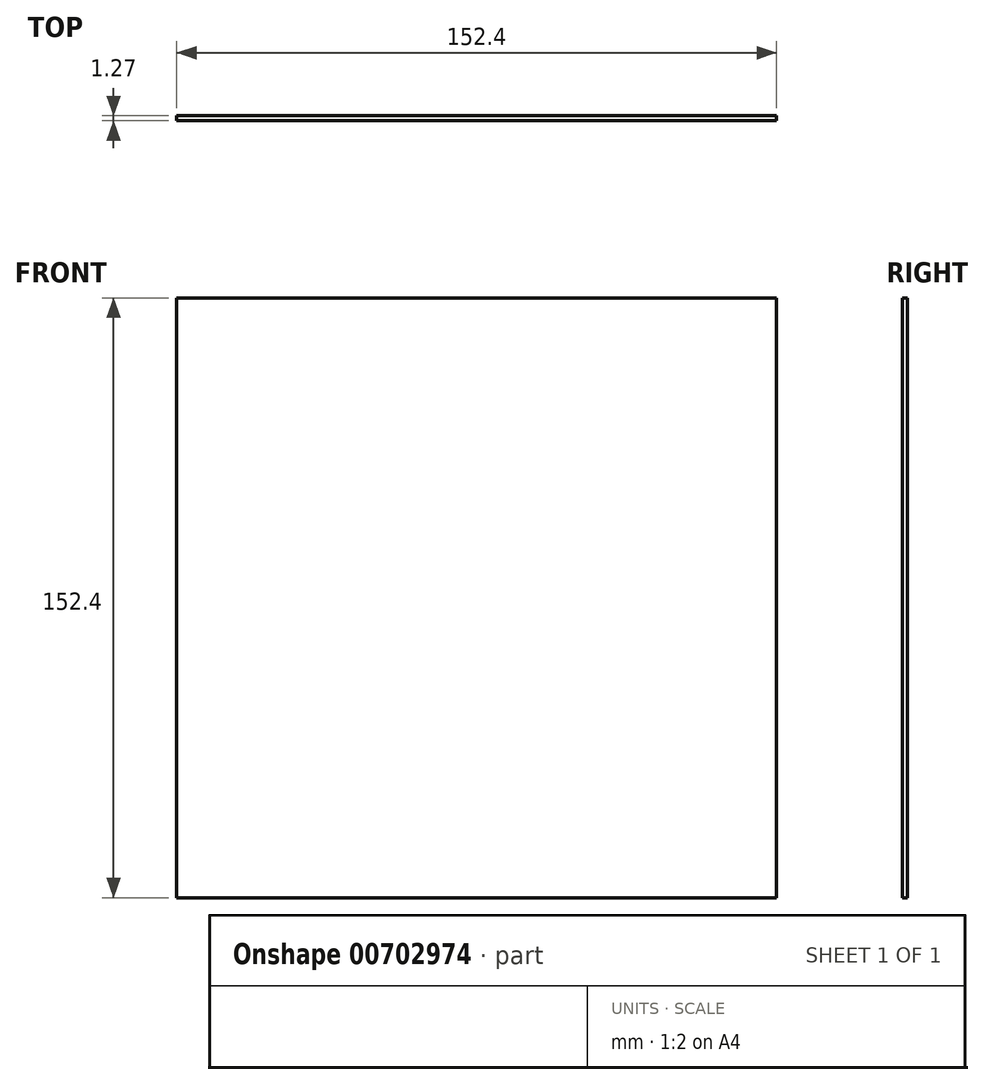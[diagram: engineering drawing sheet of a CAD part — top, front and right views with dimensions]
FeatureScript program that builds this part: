
annotation { "Feature Type Name" : "Feature", "Feature Type Description" : "" }
export const myFeature = defineFeature(function(context is Context, id is Id, definition is map)
    precondition{}
    {
        {
            var Q0;
            Q0=qCreatedBy(makeId("Front.planeOp"),FACE);
            var sketch = newSketch(context, id + "F0", { "sketchPlane" : qUnion([Q0])});
            skLineSegment(sketch, "E0.bottom", {"start": v(76.2, 76.2) * mm, "end": v(-76.2, 76.2) * mm});
            skLineSegment(sketch, "E0.top", {"start": v(76.2, -76.2) * mm, "end": v(-76.2, -76.2) * mm});
            skLineSegment(sketch, "E0.left", {"start": v(76.2, 76.2) * mm, "end": v(76.2, -76.2) * mm});
            skLineSegment(sketch, "E0.right", {"start": v(-76.2, 76.2) * mm, "end": v(-76.2, -76.2) * mm});
            skPoint(sketch, "E0.middle", {"position": v(0, 0) * mm});
            skSolve(sketch);
        }
        {
            var Q0;
            Q0 = qSketchRegion(id + "F0", true);
            extrude(context, id + "F1", {"entities" : qUnion([Q0]), "depth" : 1.27 * mm, "offsetDistance" : 25.4 * mm});
        }
    });
